# Revit family: Furniture_Other_Sjobergs_Workbench_4_Group
name_source: partatom
category: Furniture
revit_build: Autodesk Revit 2017 (Build: 20160225_1515(x64)
units: mm (PartAtom-declared; Revit-internal decimal feet)

## family parameters
Always vertical = Yes
Cut with Voids When Loaded = No
OmniClass Number = 23.40.70.14
OmniClass Title = Retail and Commercial Equipment and Furnishings
Room Calculation Point = No
Shared = No
Work Plane-Based = No

## types (1)
- 33070 Sjoberg Complete 4-Station
    AssetType = Movable
    BIMObjectName = Furniture_Other_Sjobergs_Workbench_4_Group
    Brand = Sjöbergs
    Category = School, Woodwork
    Collection = Planer Benches
    Color = Wooden
    Constituents = 33110 bench top + 33160 Front Vise + 33198 steel stand + 33201 additional board + 33142 gas springs + 33383 jaw cushions + 33384 jaw cushions + 33200 hinged stool + 33636 holdfast
    ConvergoRefNr = 0184-2005-0001-SE
    Cost = 0 $
    Description = Bench top in lacquered beech. Traditional designed and sturdily built. Bench dogs are included.
    DurationUnit = Year
    Features = This bench assembly is comprised of four Bench Tops 33110. The area of the top surface is 1600x1600 mm and the thickness is 60 mm. Bench dogs are included. There are four powerful shoulder vices in the traditional design. The vice sliding mechanism is smooth and if necessary can be easily adjusted. An optimal Sjöbergs Front Vice 33160 can be fitted to each workbench which would increase the working possibilities.
    Finish = Each top is constructed in solid, lacquered beech.
    IfcExportAs = IfcFurnishingElementType
    IfcExportType = TABLE
    MainColor = Wooden
    Manufacturer = Sjöbergs
    ManufacturerName = Sjöbergs
    ManufacturerURL = https://www.sjobergs.se
    Material = Wood, metal
    Model = 33070 Sjoberg Complete 4-Station
    ModelReference = 33070
    NBSDescription = School art, design and technology tables and workbenches;
    NBSReference = 45-35-20/320
    Name = Sjobergs_Workbench_4_Group
    NominalDepth = 1890 mm
    NominalLength = 1890 mm
    ProductDatasheet = https://www.sjobergs.se
    ProductInformation = This bench assembly is comprised of four Bench Tops 33110. Each top is constructed in solid, lacquered beech. The area of the top surface is 1600x1600 mm and the thickness is 60 mm. Bench dogs are included. There are four powerful shoulder vices in the traditional design. The vice sliding mechanism is smooth and if necessary can be easily adjusted. An optimal Sjöbergs Front Vice 33160 can be fitted to each workbench which would increase the working possibilities.
    Shape = Sculptured
    Size = 1600x1600x700-900 mm
    TableMainMaterial = Beech
    TableSecondaryMaterial = Stainless Steel
    TableTertiaryMaterial = Ash
    URL = https://www.sjobergs.se
    Uniclass2 = Pr_40_50_21
    Uniclass2015Description = Desks, Tables And Worktops
    Uniclass2015Reference = Pr_40_50_21_76
    Version = 1
    VersionDate = 26/06/2020
    WarrantyDurationUnit = Year
    Weight = 84 kg + 35 kg

## geometry (parser evidence)
native form markers: Sweep x13
no freeform markers — native parametric forms only
